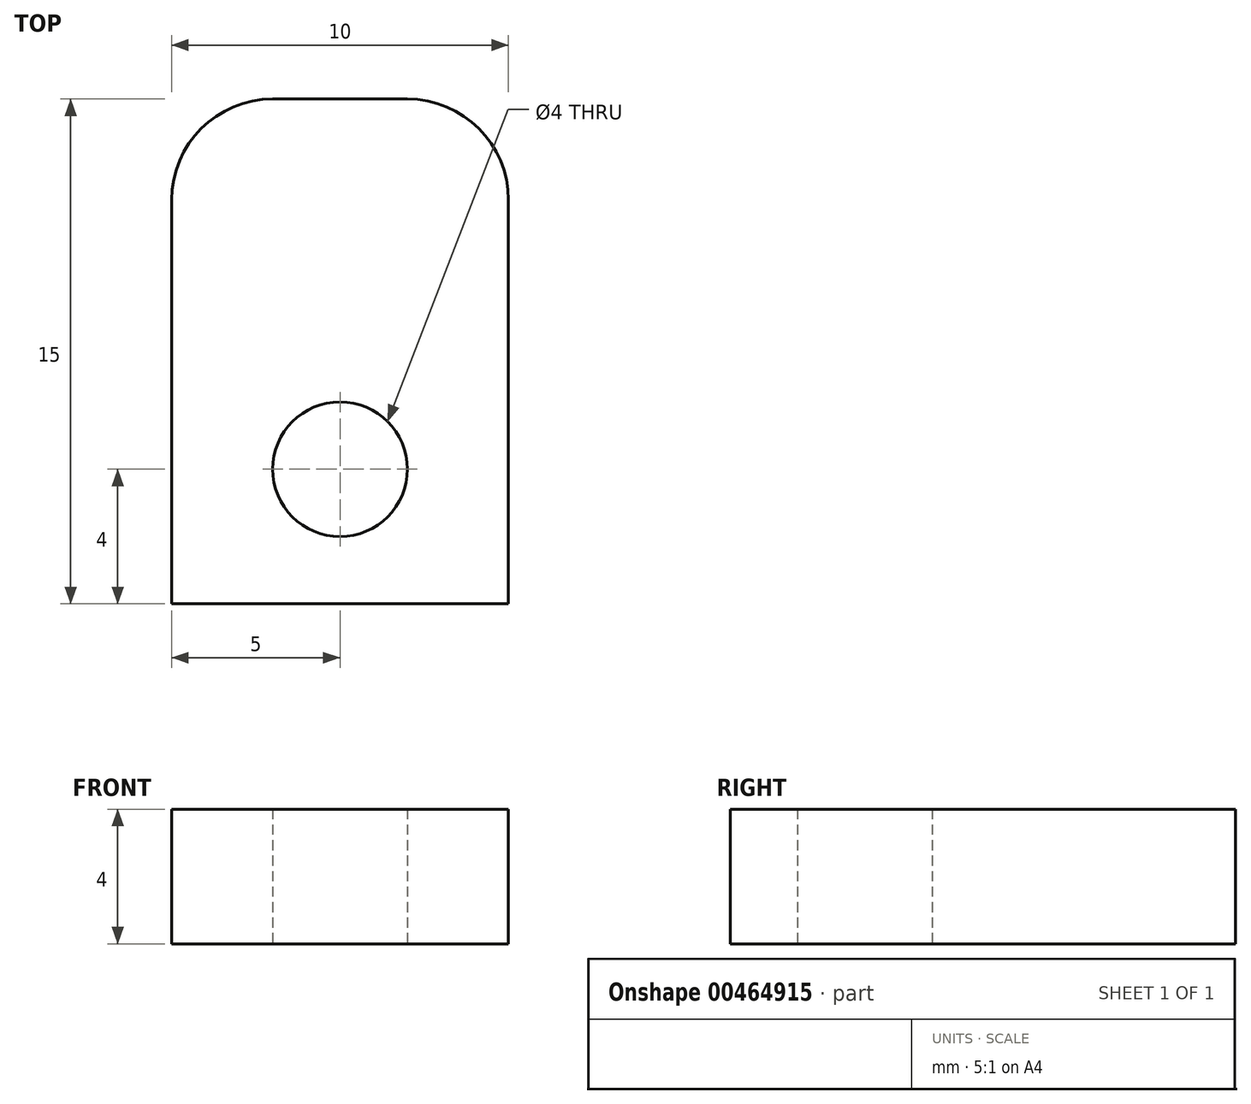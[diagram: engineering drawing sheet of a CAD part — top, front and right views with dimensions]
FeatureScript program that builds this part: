
annotation { "Feature Type Name" : "Feature", "Feature Type Description" : "" }
export const myFeature = defineFeature(function(context is Context, id is Id, definition is map)
    precondition{}
    {
        {
            var Q0;
            Q0=qCreatedBy(makeId("Top.planeOp"),FACE);
            var sketch = newSketch(context, id + "F0", { "sketchPlane" : qUnion([Q0])});
            skLineSegment(sketch, "E0.bottom", {"start": v(5, 7.5) * mm, "end": v(-5, 7.5) * mm});
            skLineSegment(sketch, "E0.top", {"start": v(5, -7.5) * mm, "end": v(-5, -7.5) * mm});
            skLineSegment(sketch, "E0.left", {"start": v(5, 7.5) * mm, "end": v(5, -7.5) * mm});
            skLineSegment(sketch, "E0.right", {"start": v(-5, 7.5) * mm, "end": v(-5, -7.5) * mm});
            skPoint(sketch, "E0.middle", {"position": v(0, 0) * mm});
            skLineSegment(sketch, "E1", {"start": v(0, -7.5) * mm, "end": v(0, -3.5) * mm});
            skPoint(sketch, "E1.endSnap0", {"position": v(0, -7.5) * mm});
            skCircle(sketch, "E2", {"center": v(0, -3.5) * mm, "radius": 2 * mm});
            skSolve(sketch);
        }
        {
            var Q0;
            Q0=makeQuery(id+"F0.imprint","IMPRINT",FACE,{"disambiguationData":[TD([[makeQuery(id+"F0.imprint","IMPRINT",EDGE,{"derivedFrom":sQuery(id+"F0.wireOp",EDGE,"E0.bottom")}),1.0]])]});
            extrude(context, id + "F1", {"entities" : qUnion([Q0]), "depth" : 4 * mm});
        }
        {
            var Q0;
            Q0=makeQuery(id+"F1.opExtrude","SWEPT_EDGE",EDGE,{"disambiguationData":[OSD([sQuery(id+"F0.wireOp",EDGE,"E0.bottom"),sQuery(id+"F0.wireOp",EDGE,"E0.right")])]});
            var Q1;
            Q1=makeQuery(id+"F1.opExtrude","SWEPT_EDGE",EDGE,{"disambiguationData":[OSD([sQuery(id+"F0.wireOp",EDGE,"E0.bottom"),sQuery(id+"F0.wireOp",EDGE,"E0.left")])]});
            fillet(context, id + "F2", {"entities" : qUnion([Q0, Q1]), "radius" : 3 * mm, "tangentPropagation" : true, "allowEdgeOverflow" : false});
        }
    });
